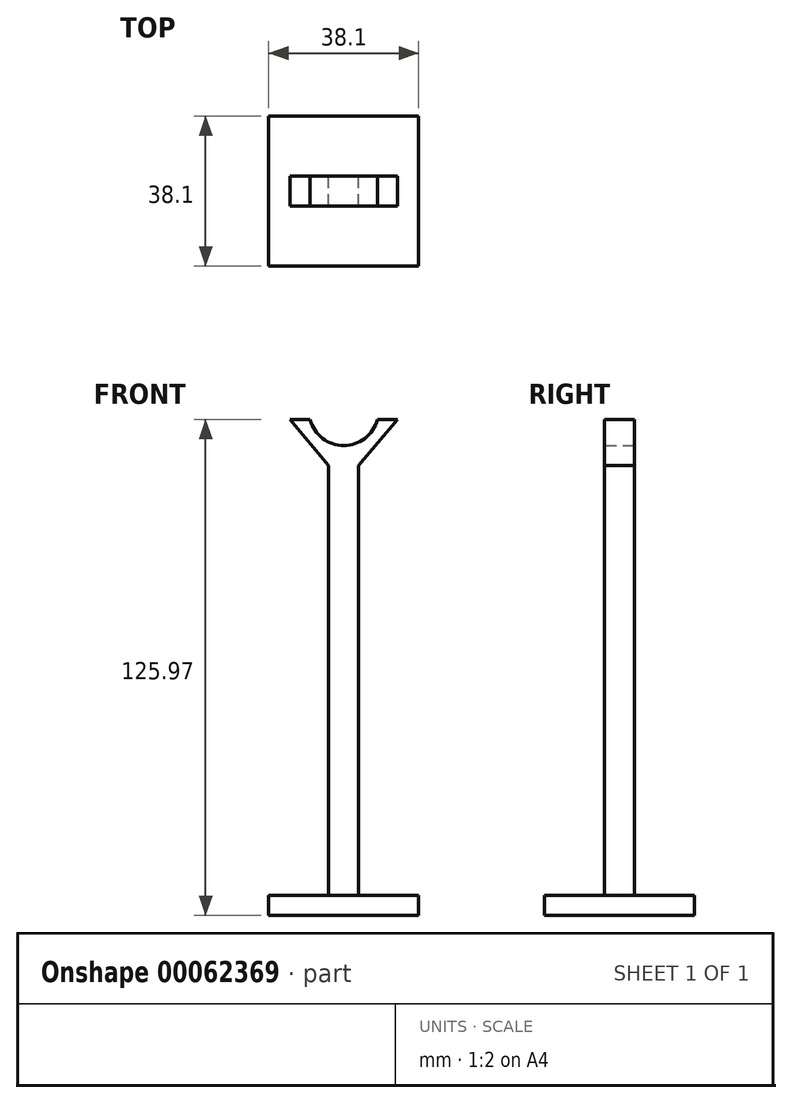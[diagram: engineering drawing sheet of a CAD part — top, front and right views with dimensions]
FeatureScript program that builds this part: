
annotation { "Feature Type Name" : "Feature", "Feature Type Description" : "" }
export const myFeature = defineFeature(function(context is Context, id is Id, definition is map)
    precondition{}
    {
        {
            var Q0;
            Q0=qCreatedBy(makeId("Front.planeOp"),FACE);
            var sketch = newSketch(context, id + "F0", { "sketchPlane" : qUnion([Q0])});
            skLineSegment(sketch, "E0.rect.bottom", {"start": v(3.8, 57.15) * mm, "end": v(-3.81, 57.15) * mm});
            skLineSegment(sketch, "E0.rect.top", {"start": v(3.81, -57.15) * mm, "end": v(-3.8, -57.15) * mm});
            skLineSegment(sketch, "E0.rect.left", {"start": v(3.8, 57.15) * mm, "end": v(3.81, -57.15) * mm});
            skLineSegment(sketch, "E0.rect.right", {"start": v(-3.81, 57.15) * mm, "end": v(-3.8, -57.15) * mm});
            skPoint(sketch, "E0.rect.middle", {"position": v(0, 0) * mm});
            skLineSegment(sketch, "E1", {"start": v(-3.81, 57.15) * mm, "end": v(-13.6, 68.82) * mm});
            skLineSegment(sketch, "E2", {"start": v(-13.6, 68.82) * mm, "end": v(-8.53, 68.82) * mm});
            skLineSegment(sketch, "E3", {"start": v(3.8, 57.15) * mm, "end": v(13.6, 68.82) * mm});
            skLineSegment(sketch, "E4", {"start": v(13.6, 68.82) * mm, "end": v(8.53, 68.82) * mm});
            skArc(sketch, "E5", {"start": v(-8.53, 68.82) * mm, "mid": v(0, 62.23) * mm, "end": v(8.53, 68.82) * mm});
            skSolve(sketch);
        }
        {
            var Q0;
            Q0 = qSketchRegion(id + "F0", true);
            extrude(context, id + "F1", {"entities" : qUnion([Q0]), "endBound" : BoundingType.SYMMETRIC, "depth" : 7.62 * mm});
        }
        {
            var Q0;
            Q0=makeQuery(id+"F1.opExtrude","SWEPT_FACE",FACE,{"disambiguationData":[OSD([sQuery(id+"F0.wireOp",EDGE,"E0.rect.top")])]});
            var sketch = newSketch(context, id + "F2", { "sketchPlane" : qUnion([Q0])});
            skLineSegment(sketch, "E6.rect.bottom", {"start": v(19.05, 19.05) * mm, "end": v(-19.05, 19.05) * mm});
            skLineSegment(sketch, "E6.rect.top", {"start": v(19.05, -19.05) * mm, "end": v(-19.05, -19.05) * mm});
            skLineSegment(sketch, "E6.rect.left", {"start": v(19.05, 19.05) * mm, "end": v(19.05, -19.05) * mm});
            skLineSegment(sketch, "E6.rect.right", {"start": v(-19.05, 19.05) * mm, "end": v(-19.05, -19.05) * mm});
            skPoint(sketch, "E6.rect.middle", {"position": v(0, 0) * mm});
            skSolve(sketch);
        }
        {
            var Q0;
            Q0=makeQuery(id+"F2.imprint","IMPRINT",FACE,{"disambiguationData":[TD([[makeQuery(id+"F2.imprint","IMPRINT",EDGE,{"derivedFrom":sQuery(id+"F2.wireOp",EDGE,"E6.rect.bottom")}),1.0]])]});
            extrude(context, id + "F3", {"entities" : qUnion([Q0]), "operationType" : NewBodyOperationType.ADD, "oppositeDirection" : true, "depth" : 5.08 * mm});
        }
    });
